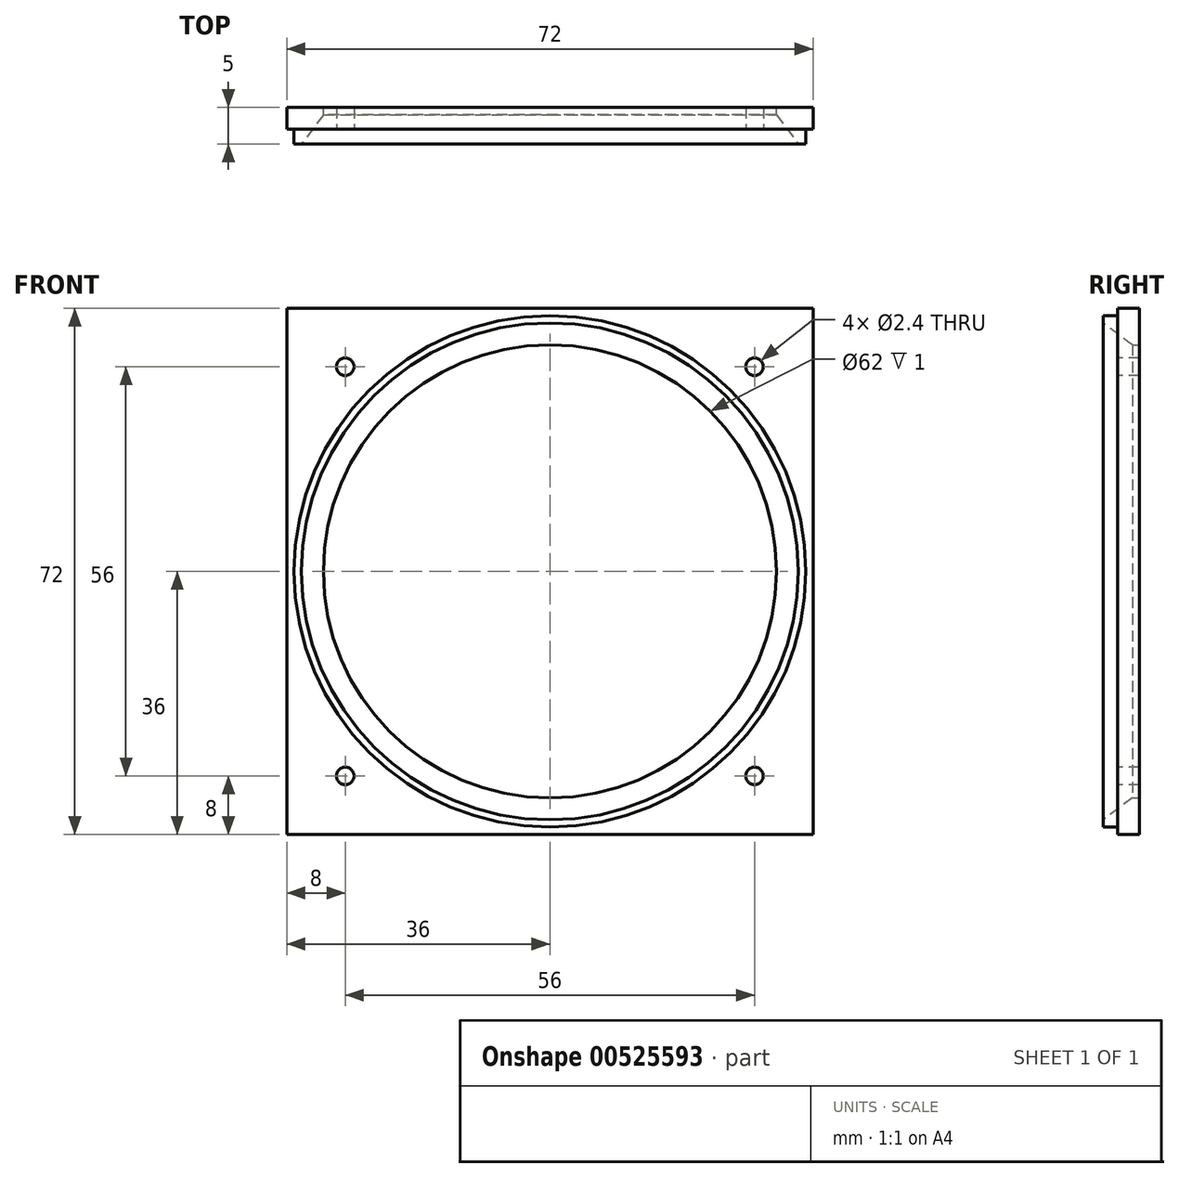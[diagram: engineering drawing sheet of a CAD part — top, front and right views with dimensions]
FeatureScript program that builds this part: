
annotation { "Feature Type Name" : "Feature", "Feature Type Description" : "" }
export const myFeature = defineFeature(function(context is Context, id is Id, definition is map)
    precondition{}
    {
        {
            var Q0;
            Q0=qCreatedBy(makeId("Right.planeOp"),FACE);
            var sketch = newSketch(context, id + "F0", { "sketchPlane" : qUnion([Q0])});
            skLineSegment(sketch, "E0", {"start": v(19.32, 0) * mm, "end": v(-16.11, 0) * mm, "construction": true});
            skLineSegment(sketch, "E1", {"start": v(-3, 35) * mm, "end": v(-3, 34) * mm});
            skLineSegment(sketch, "E2", {"start": v(2, 31) * mm, "end": v(2, 35) * mm});
            skLineSegment(sketch, "E3", {"start": v(2, 35) * mm, "end": v(-3, 35) * mm});
            skLineSegment(sketch, "E4", {"start": v(2, 31) * mm, "end": v(1, 31) * mm});
            skLineSegment(sketch, "E5", {"start": v(1, 31) * mm, "end": v(-3, 34) * mm});
            skSolve(sketch);
        }
        {
            var Q0;
            Q0=qSketchRegion(id+"F0",true);
            var Q1;
            Q1=sQuery(id+"F0.wireOp",EDGE,"E0");
            revolve(context, id + "F1", {"entities" : qUnion([Q0]), "axis" : qUnion([Q1]), "revolveType" : RevolveType.FULL});
        }
        {
            var Q0;
            Q0=makeQuery(id+"F1.opRevolve","SWEPT_FACE",FACE,{"disambiguationData":[OSD([sQuery(id+"F0.wireOp",EDGE,"E1")])]});
            cPlane(context, id + "F2", {"entities" : qUnion([Q0]), "cplaneType" : CPlaneType.OFFSET, "offset" : 2 * mm, "oppositeDirection" : true, "width" : 150 * mm, "height" : 150 * mm});
        }
        {
            var Q0;
            Q0=qCreatedBy(id+"F2.planeOp",FACE);
            var sketch = newSketch(context, id + "F3", { "sketchPlane" : qUnion([Q0])});
            skPoint(sketch, "E6.middle", {"position": v(0, 0) * mm});
            skCircle(sketch, "E7", {"center": v(-28, 28) * mm, "radius": 1.2 * mm});
            skCircle(sketch, "E8", {"center": v(-28, -28) * mm, "radius": 1.2 * mm});
            skCircle(sketch, "E9", {"center": v(28, -28) * mm, "radius": 1.2 * mm});
            skCircle(sketch, "E10", {"center": v(28, 28) * mm, "radius": 1.2 * mm});
            skCircle(sketch, "E11", {"center": v(0, 0) * mm, "radius": 35 * mm});
            skLineSegment(sketch, "E12.bottom", {"start": v(36, -36) * mm, "end": v(-36, -36) * mm});
            skLineSegment(sketch, "E12.top", {"start": v(36, 36) * mm, "end": v(-36, 36) * mm});
            skLineSegment(sketch, "E12.left", {"start": v(36, -36) * mm, "end": v(36, 36) * mm});
            skLineSegment(sketch, "E12.right", {"start": v(-36, -36) * mm, "end": v(-36, 36) * mm});
            skSolve(sketch);
        }
        {
            var Q0;
            Q0=qSketchRegion(id+"F3",true);
            extrude(context, id + "F4", {"entities" : qUnion([Q0]), "operationType" : NewBodyOperationType.ADD, "oppositeDirection" : true, "depth" : 3 * mm, "offsetDistance" : 25 * mm});
        }
    });
